# Revit family: Clarus_Divide Thinline_Center Clamp_R18
name_source: partatom
category: Furniture
revit_build: Autodesk Revit 2018 (Build: 20190510_1515(x64)
units: mm (PartAtom-declared; Revit-internal decimal feet)

## family parameters
Cut with Voids When Loaded = No
Host = Face
Room Calculation Point = No
Shared = No

## types (1)
- 6" Clamp - 48" Width
    Clamp Width = 6"
    Default Elevation = 0"
    Description = Buckle down on your workspace challenges with Divide ThinLine from Clarus®. This beautifully
engineered desk divider system boasts clean lines that won’t harm your existing offi ce furniture.
Since no drilling is involved and all hardware screws are strategically hidden inside the clamps,
Divide ThinLine seamlessly integrates and reduces visual distractions in your offi ce, all while
maintaining the overall aesthetic. Using this new patent pending state-of-the-art clamping system,
Divide ThinLine can be easily installed at the back, side or along the center of a desk, giving you the
freedom to accommodate power cords, monitor arm att achments and more. You have the option to
mix and match ThinLine Top, ThinLine Side and ThinLine Center hardware on the same table, which
allows you to uniquely divide up your offi ce with stability and style.
    Edge Offset = 0"
    Glass Thickness = 1/4"
    Height = 18"
    Height Control = 18"
    Manufacturer = Clarus
    Model = Divide ThinLine
    Modeled By = Commense Studio
    Product URL = https://www.clarus.com
    URL = https://www.clarus.com
    Width = 48"

## geometry (parser evidence)
native form markers: Blend x2, Sweep x6
no freeform markers — native parametric forms only
